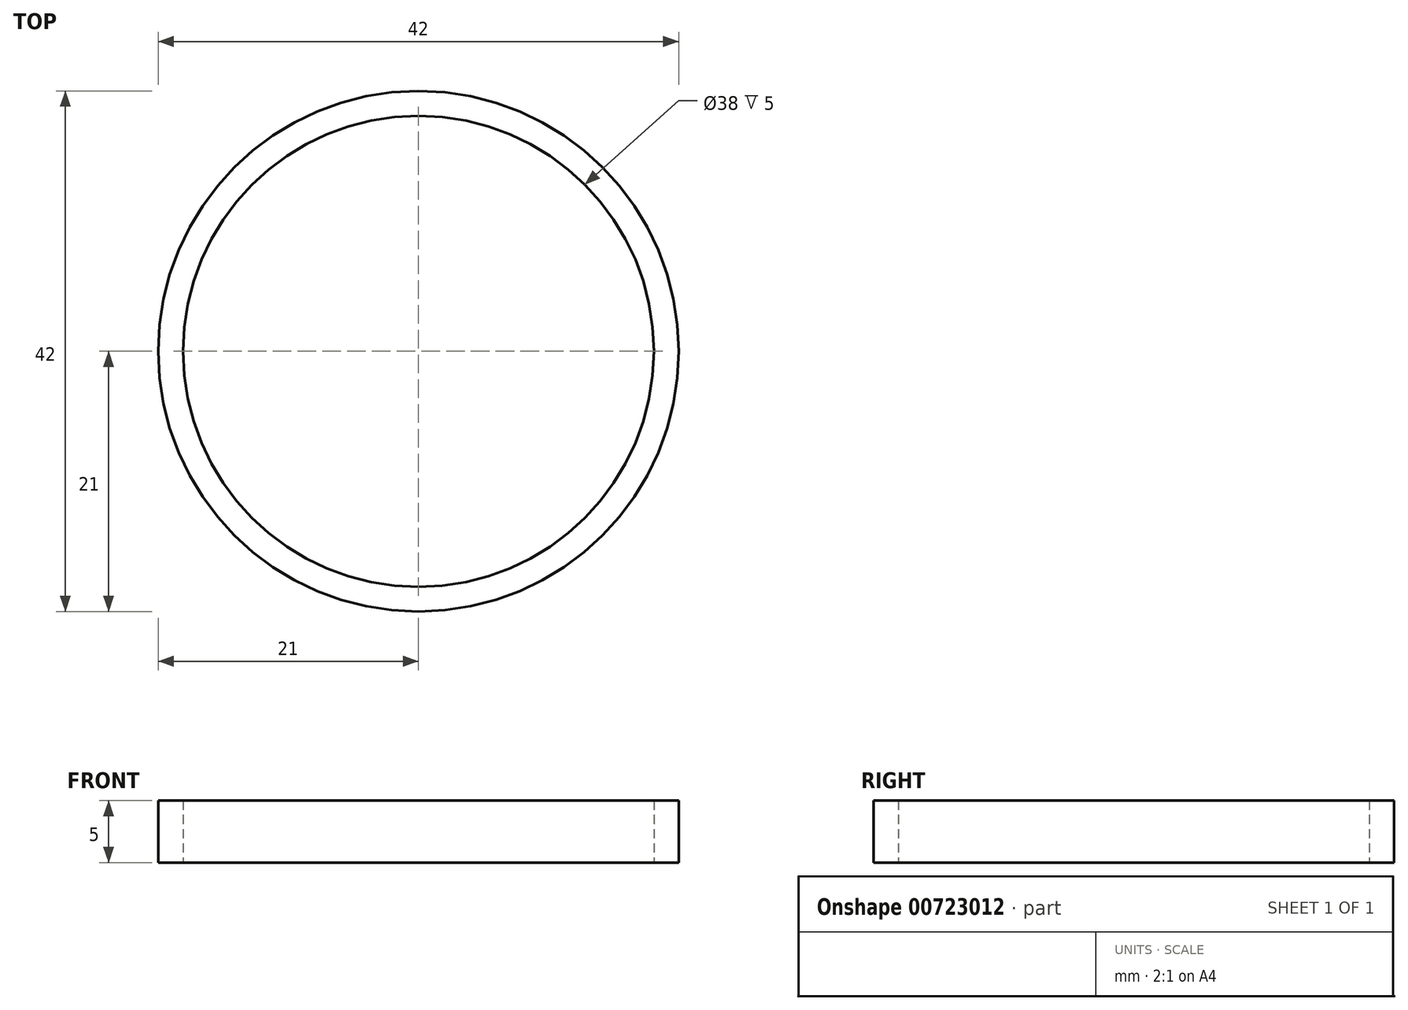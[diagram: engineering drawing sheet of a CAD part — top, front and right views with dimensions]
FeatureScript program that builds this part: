
annotation { "Feature Type Name" : "Feature", "Feature Type Description" : "" }
export const myFeature = defineFeature(function(context is Context, id is Id, definition is map)
    precondition{}
    {
        {
            var Q0;
            Q0=qCreatedBy(makeId("Top.planeOp"),FACE);
            var sketch = newSketch(context, id + "F0", { "sketchPlane" : qUnion([Q0])});
            skCircle(sketch, "E0", {"center": v(0, 0) * mm, "radius": 19 * mm});
            skCircle(sketch, "E1", {"center": v(0, 0) * mm, "radius": 21 * mm});
            skSolve(sketch);
        }
        {
            var Q0;
            Q0 = qSketchRegion(id + "F0", true);
            extrude(context, id + "F1", {"entities" : qUnion([Q0]), "depth" : 5 * mm, "offsetDistance" : 25 * mm});
        }
    });
